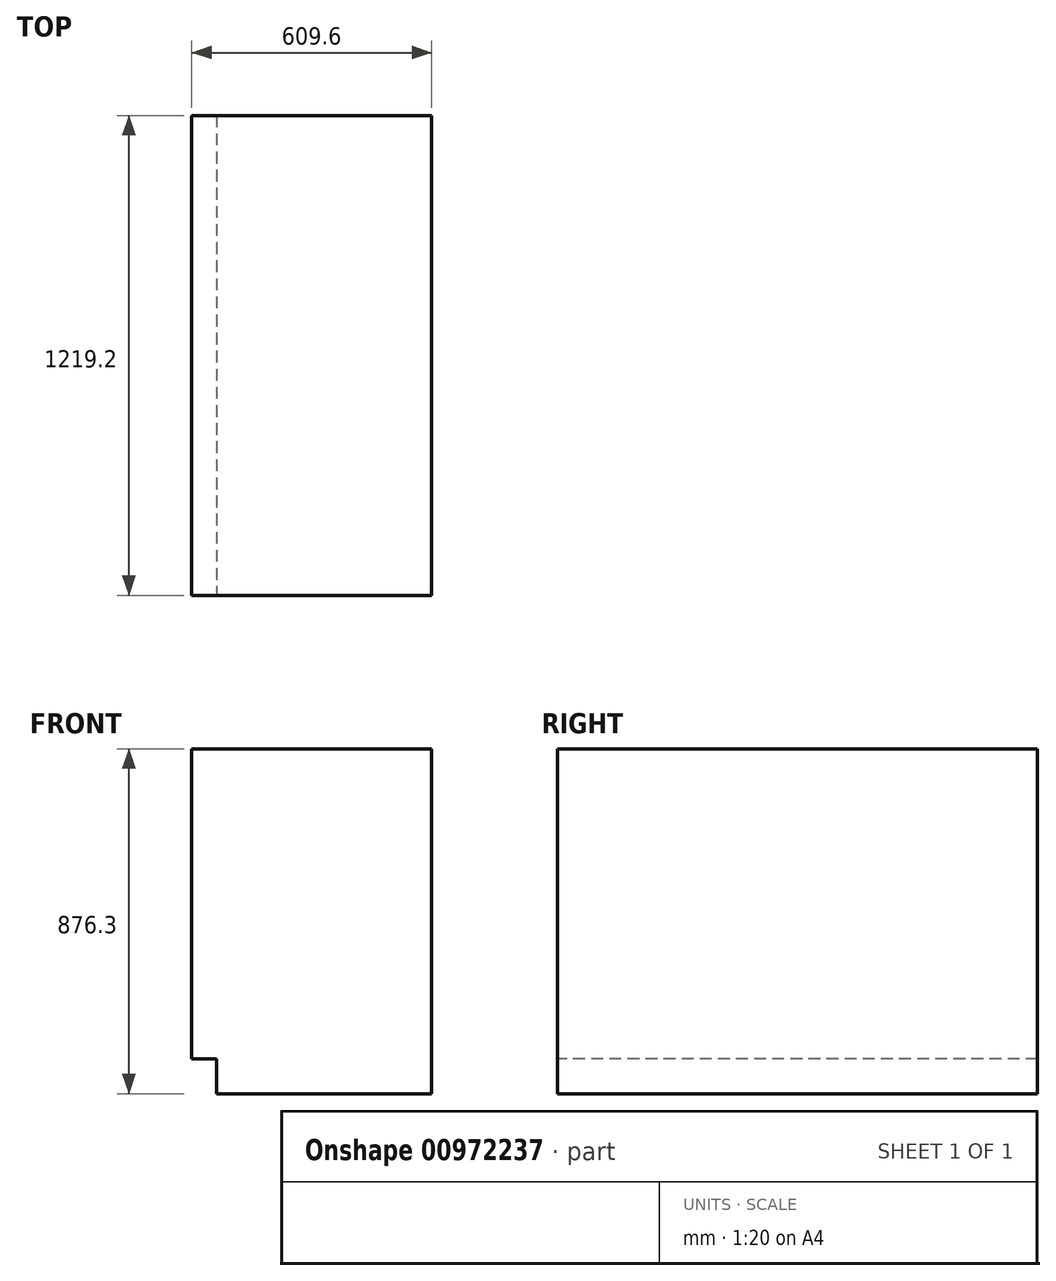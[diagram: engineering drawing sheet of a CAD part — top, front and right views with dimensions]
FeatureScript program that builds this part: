
annotation { "Feature Type Name" : "Feature", "Feature Type Description" : "" }
export const myFeature = defineFeature(function(context is Context, id is Id, definition is map)
    precondition{}
    {
        {
            var Q0;
            Q0=qCreatedBy(makeId("Front.planeOp"),FACE);
            var sketch = newSketch(context, id + "F0", { "sketchPlane" : qUnion([Q0])});
            skLineSegment(sketch, "E0", {"start": v(0, 0) * mm, "end": v(0, 876.3) * mm});
            skLineSegment(sketch, "E1", {"start": v(0, 0) * mm, "end": v(-546.1, 0) * mm});
            skLineSegment(sketch, "E2", {"start": v(-546.1, 0) * mm, "end": v(-546.1, 88.9) * mm});
            skLineSegment(sketch, "E3", {"start": v(-546.1, 88.9) * mm, "end": v(-609.6, 88.9) * mm});
            skLineSegment(sketch, "E4", {"start": v(-609.6, 88.9) * mm, "end": v(-609.6, 876.3) * mm});
            skLineSegment(sketch, "E5", {"start": v(0, 876.3) * mm, "end": v(-609.6, 876.3) * mm});
            skSolve(sketch);
        }
        {
            var Q0;
            Q0=makeQuery(id+"F0.imprint","IMPRINT",FACE,{"disambiguationData":[TD([[makeQuery(id+"F0.imprint","IMPRINT",EDGE,{"derivedFrom":sQuery(id+"F0.wireOp",EDGE,"E0")}),1.0]])]});
            extrude(context, id + "F1", {"entities" : qUnion([Q0]), "oppositeDirection" : true, "depth" : 1219.2 * mm, "offsetDistance" : 25.4 * mm});
        }
    });
